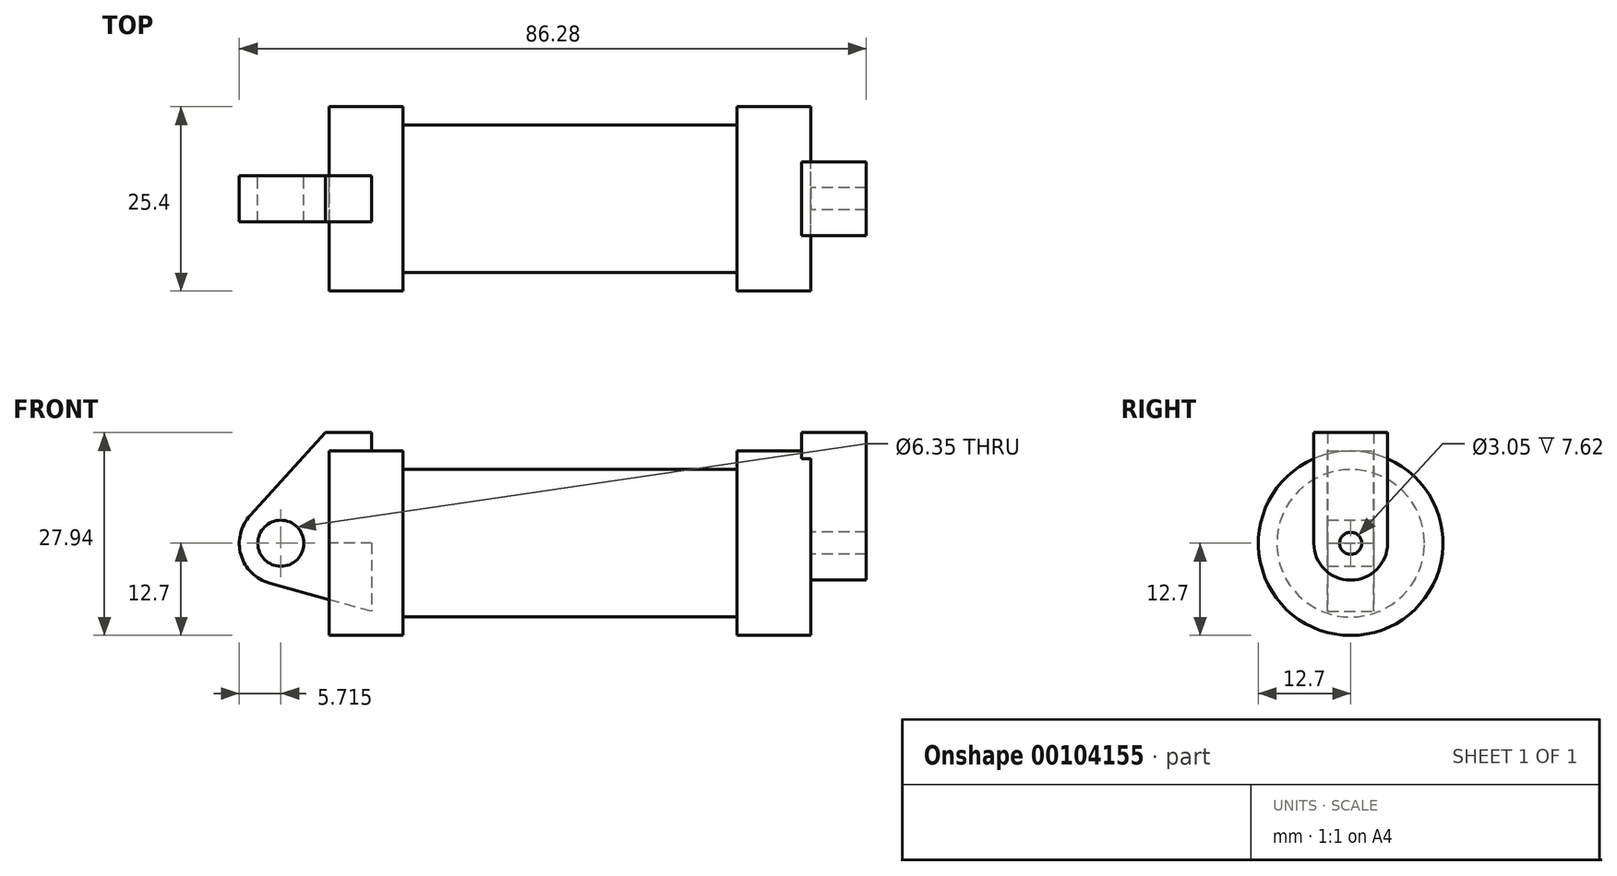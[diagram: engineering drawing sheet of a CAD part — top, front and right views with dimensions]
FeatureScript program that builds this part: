
annotation { "Feature Type Name" : "Feature", "Feature Type Description" : "" }
export const myFeature = defineFeature(function(context is Context, id is Id, definition is map)
    precondition{}
    {
        {
            var Q0;
            Q0=qCreatedBy(makeId("Front.planeOp"),FACE);
            var sketch = newSketch(context, id + "F0", { "sketchPlane" : qUnion([Q0])});
            skLineSegment(sketch, "E0", {"start": v(0, 0) * mm, "end": v(0, 12.7) * mm});
            skLineSegment(sketch, "E1", {"start": v(0, 12.7) * mm, "end": v(10.16, 12.7) * mm});
            skLineSegment(sketch, "E2", {"start": v(10.16, 12.7) * mm, "end": v(10.16, 10.16) * mm});
            skLineSegment(sketch, "E3", {"start": v(10.16, 10.16) * mm, "end": v(56.13, 10.16) * mm});
            skLineSegment(sketch, "E4", {"start": v(56.13, 10.16) * mm, "end": v(56.13, 12.7) * mm});
            skLineSegment(sketch, "E5", {"start": v(56.13, 12.7) * mm, "end": v(66.3, 12.7) * mm});
            skLineSegment(sketch, "E6", {"start": v(66.3, 12.7) * mm, "end": v(66.3, 0) * mm});
            skLineSegment(sketch, "E7", {"start": v(66.3, 0) * mm, "end": v(0, 0) * mm});
            skLineSegment(sketch, "E8", {"start": v(5.84, 15.24) * mm, "end": v(-0.5, 15.24) * mm});
            skLineSegment(sketch, "E9", {"start": v(-0.5, 15.24) * mm, "end": v(-10.88, 3.85) * mm});
            skLineSegment(sketch, "E10", {"start": v(0, 0) * mm, "end": v(-6.65, 0) * mm});
            skCircle(sketch, "E11", {"center": v(-6.65, 0) * mm, "radius": 5.72 * mm});
            skCircle(sketch, "E12", {"center": v(-6.65, 0) * mm, "radius": 3.18 * mm});
            skLineSegment(sketch, "E13", {"start": v(5.84, 15.24) * mm, "end": v(5.84, -9.4) * mm});
            skLineSegment(sketch, "E14", {"start": v(5.84, -9.4) * mm, "end": v(-8.18, -5.5) * mm});
            skSolve(sketch);
        }
        {
            var Q0;
            {var subQ0=sQuery(id+"F0.wireOp",EDGE,"E0");Q0=makeQuery(id+"F0.imprint","IMPRINT",FACE,{"disambiguationData":[TD([[makeQuery(id+"F0.imprint","IMPRINT",EDGE,{"derivedFrom":subQ0}),-1.0]])]});}
            var Q1;
            {var subQ0=sQuery(id+"F0.wireOp",EDGE,"E2");Q1=makeQuery(id+"F0.imprint","IMPRINT",FACE,{"disambiguationData":[TD([[makeQuery(id+"F0.imprint","IMPRINT",EDGE,{"derivedFrom":subQ0}),-1.0]])]});}
            var Q2;
            Q2=sQuery(id+"F0.wireOp",EDGE,"E7");
            revolve(context, id + "F1", {"entities" : qUnion([Q0, Q1]), "axis" : qUnion([Q2]), "revolveType" : RevolveType.FULL});
        }
        {
            var Q0;
            {var subQ4=sQuery(id+"F0.wireOp",EDGE,"E12");Q0=makeQuery(id+"F0.imprint","IMPRINT",FACE,{"disambiguationData":[TD([[makeQuery(id+"F0.imprint","IMPRINT",EDGE,{"derivedFrom":subQ4}),-1.0]])]});}
            var Q1;
            {var subQ3=sQuery(id+"F0.wireOp",EDGE,"E0");Q1=makeQuery(id+"F0.imprint","IMPRINT",FACE,{"disambiguationData":[TD([[makeQuery(id+"F0.imprint","IMPRINT",EDGE,{"derivedFrom":subQ3}),1.0]])]});}
            var Q2;
            {var subQ0=sQuery(id+"F0.wireOp",EDGE,"E14");Q2=makeQuery(id+"F0.imprint","IMPRINT",FACE,{"disambiguationData":[TD([[makeQuery(id+"F0.imprint","IMPRINT",EDGE,{"derivedFrom":subQ0}),-1.0]])]});}
            extrude(context, id + "F2", {"entities" : qUnion([Q0, Q1, Q2]), "endBound" : BoundingType.SYMMETRIC, "depth" : 6.35 * mm});
        }
        {
            var Q0;
            Q0=makeQuery(id+"F1.opRevolve","SWEPT_FACE",FACE,{"disambiguationData":[OSD([sQuery(id+"F0.wireOp",EDGE,"E6")])]});
            var sketch = newSketch(context, id + "F3", { "sketchPlane" : qUnion([Q0])});
            skCircle(sketch, "E15", {"center": v(0, 0) * mm, "radius": 1.52 * mm});
            skCircle(sketch, "E16", {"center": v(0, 0) * mm, "radius": 5.08 * mm});
            skLineSegment(sketch, "E17", {"start": v(0, 0) * mm, "end": v(5.08, 0) * mm, "construction": true});
            skLineSegment(sketch, "E18", {"start": v(5.08, 0) * mm, "end": v(5.08, 15.24) * mm});
            skLineSegment(sketch, "E19", {"start": v(-5.08, 0) * mm, "end": v(-5.08, 15.24) * mm});
            skLineSegment(sketch, "E20", {"start": v(-5.08, 15.24) * mm, "end": v(5.08, 15.24) * mm});
            skLineSegment(sketch, "E21", {"start": v(0, 0) * mm, "end": v(-5.08, 0) * mm, "construction": true});
            skSolve(sketch);
        }
        {
            var Q0;
            Q0 = qSketchRegion(id + "F3", true);
            extrude(context, id + "F4", {"entities" : qUnion([Q0]), "operationType" : NewBodyOperationType.ADD, "depth" : 7.62 * mm});
        }
        {
            var Q0;
            Q0=makeQuery(id+"F4.opExtrude","CAP_FACE",FACE,{"disambiguationData":[OSD([sQuery(id+"F3.wireOp",EDGE,"E15"),sQuery(id+"F3.wireOp",EDGE,"E16"),sQuery(id+"F3.wireOp",EDGE,"E18"),sQuery(id+"F3.wireOp",EDGE,"E19"),sQuery(id+"F3.wireOp",EDGE,"E20")])],"isStart":true});
            extrude(context, id + "F5", {"entities" : qUnion([Q0]), "operationType" : NewBodyOperationType.ADD, "depth" : 1.27 * mm});
        }
    });
